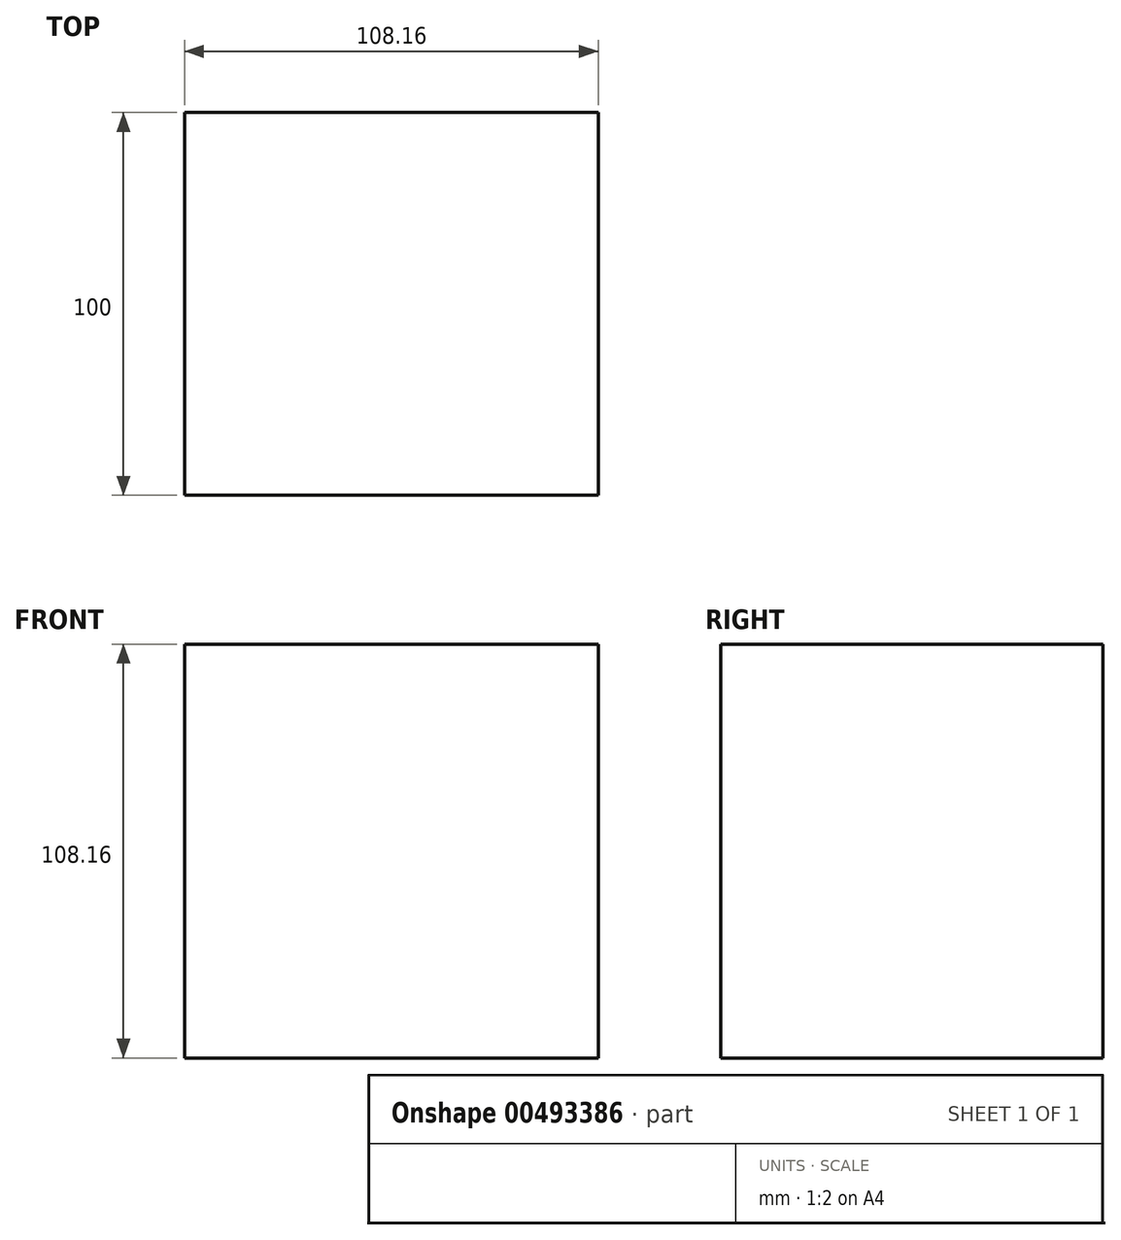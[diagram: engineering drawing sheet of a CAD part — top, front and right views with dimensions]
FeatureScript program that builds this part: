
annotation { "Feature Type Name" : "Feature", "Feature Type Description" : "" }
export const myFeature = defineFeature(function(context is Context, id is Id, definition is map)
    precondition{}
    {
        {
            var Q0;
            Q0=qCreatedBy(makeId("Front.planeOp"),FACE);
            var sketch = newSketch(context, id + "F0", { "sketchPlane" : qUnion([Q0])});
            skCircle(sketch, "E0.cCircle", {"center": v(0, 0) * mm, "radius": 54.08 * mm, "construction": true});
            skLineSegment(sketch, "E0.0", {"start": v(-54.08, 54.08) * mm, "end": v(54.08, 54.08) * mm});
            skLineSegment(sketch, "E0.1", {"start": v(54.08, 54.08) * mm, "end": v(54.08, -54.08) * mm});
            skLineSegment(sketch, "E0.2", {"start": v(54.08, -54.08) * mm, "end": v(-54.08, -54.08) * mm});
            skLineSegment(sketch, "E0.3", {"start": v(-54.08, -54.08) * mm, "end": v(-54.08, 54.08) * mm});
            skPoint(sketch, "E0.0.midPoint", {"position": v(0, 54.08) * mm});
            skSolve(sketch);
        }
        {
            var Q0;
            Q0=makeQuery(id+"F0.imprint","IMPRINT",FACE,{"disambiguationData":[TD([[makeQuery(id+"F0.imprint","IMPRINT",EDGE,{"derivedFrom":sQuery(id+"F0.wireOp",EDGE,"E0.0")}),-1.0]])]});
            extrude(context, id + "F1", {"entities" : qUnion([Q0]), "endBound" : BoundingType.SYMMETRIC, "depth" : 100 * mm});
        }
    });
